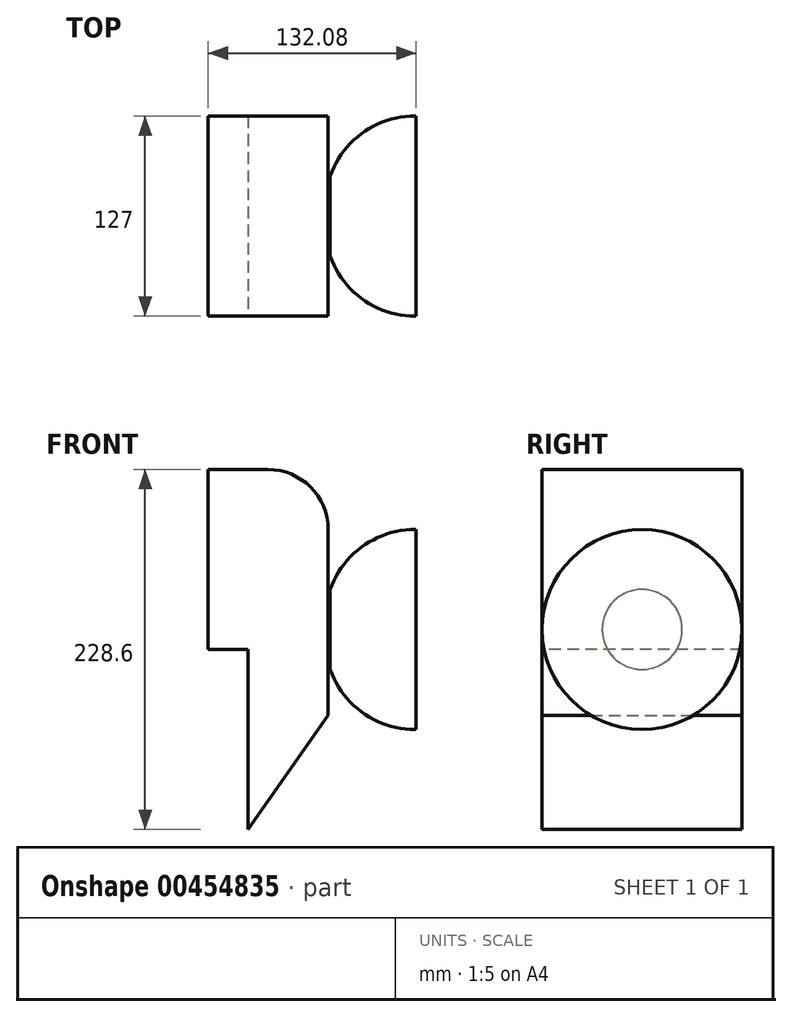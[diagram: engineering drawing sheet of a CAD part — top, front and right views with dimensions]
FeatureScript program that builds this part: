
annotation { "Feature Type Name" : "Feature", "Feature Type Description" : "" }
export const myFeature = defineFeature(function(context is Context, id is Id, definition is map)
    precondition{}
    {
        {
            var Q0;
            Q0=qCreatedBy(makeId("Right.planeOp"),FACE);
            var sketch = newSketch(context, id + "F0", { "sketchPlane" : qUnion([Q0])});
            skLineSegment(sketch, "E0.bottom", {"start": v(63.5, 114.3) * mm, "end": v(-63.5, 114.3) * mm});
            skLineSegment(sketch, "E0.top", {"start": v(63.5, -114.3) * mm, "end": v(-63.5, -114.3) * mm});
            skLineSegment(sketch, "E0.left", {"start": v(63.5, 114.3) * mm, "end": v(63.5, -114.3) * mm});
            skLineSegment(sketch, "E0.right", {"start": v(-63.5, 114.3) * mm, "end": v(-63.5, -114.3) * mm});
            skPoint(sketch, "E0.middle", {"position": v(0, 0) * mm});
            skSolve(sketch);
        }
        {
            var Q0;
            Q0 = qSketchRegion(id + "F0", true);
            extrude(context, id + "F1", {"entities" : qUnion([Q0]), "depth" : 50.8 * mm, "offsetDistance" : 25.4 * mm});
        }
        {
            var Q0;
            Q0=makeQuery(id+"F1.opExtrude","CAP_EDGE",EDGE,{"disambiguationData":[OSD([sQuery(id+"F0.wireOp",EDGE,"E0.bottom")])],"isStart":false});
            fillet(context, id + "F2", {"entities" : qUnion([Q0]), "radius" : 38.1 * mm, "tangentPropagation" : true, "allowEdgeOverflow" : false});
        }
        {
            var Q0;
            Q0=makeQuery(id+"F1.opExtrude","CAP_EDGE",EDGE,{"disambiguationData":[OSD([sQuery(id+"F0.wireOp",EDGE,"E0.top")])],"isStart":false});
            chamfer(context, id + "F3", {"entities" : qUnion([Q0]), "chamferType" : ChamferType.OFFSET_ANGLE, "width" : 50.8 * mm, "oppositeDirection" : false, "angle" : 55 * degree, "tangentPropagation" : true});
        }
        {
            var Q0;
            Q0=makeQuery(id+"F1.opExtrude","CAP_FACE",FACE,{"disambiguationData":[OSD([sQuery(id+"F0.wireOp",EDGE,"E0.bottom"),sQuery(id+"F0.wireOp",EDGE,"E0.top"),sQuery(id+"F0.wireOp",EDGE,"E0.left"),sQuery(id+"F0.wireOp",EDGE,"E0.right")])],"isStart":true});
            var sketch = newSketch(context, id + "F4", { "sketchPlane" : qUnion([Q0])});
            skLineSegment(sketch, "E1.bottom", {"start": v(-63.5, 114.3) * mm, "end": v(63.5, 114.3) * mm});
            skLineSegment(sketch, "E1.top", {"start": v(-63.5, 101.6) * mm, "end": v(63.5, 101.6) * mm});
            skLineSegment(sketch, "E1.left", {"start": v(-63.5, 114.3) * mm, "end": v(-63.5, 101.6) * mm});
            skLineSegment(sketch, "E1.right", {"start": v(63.5, 114.3) * mm, "end": v(63.5, 101.6) * mm});
            skSolve(sketch);
        }
        {
            var Q0;
            Q0 = qSketchRegion(id + "F4", true);
            extrude(context, id + "F5", {"entities" : qUnion([Q0]), "operationType" : NewBodyOperationType.ADD, "depth" : 25.4 * mm, "offsetDistance" : 25.4 * mm});
        }
        {
            var Q0;
            Q0=makeQuery(id+"F1.opExtrude","CAP_FACE",FACE,{"disambiguationData":[OSD([sQuery(id+"F0.wireOp",EDGE,"E0.bottom"),sQuery(id+"F0.wireOp",EDGE,"E0.top"),sQuery(id+"F0.wireOp",EDGE,"E0.left"),sQuery(id+"F0.wireOp",EDGE,"E0.right")])],"isStart":true});
            var sketch = newSketch(context, id + "F6", { "sketchPlane" : qUnion([Q0])});
            skLineSegment(sketch, "E2.bottom", {"start": v(-63.5, 101.6) * mm, "end": v(63.5, 101.6) * mm});
            skLineSegment(sketch, "E2.top", {"start": v(-63.5, 0) * mm, "end": v(63.5, 0) * mm});
            skLineSegment(sketch, "E2.left", {"start": v(-63.5, 101.6) * mm, "end": v(-63.5, 0) * mm});
            skLineSegment(sketch, "E2.right", {"start": v(63.5, 101.6) * mm, "end": v(63.5, 0) * mm});
            skSolve(sketch);
        }
        {
            var Q0;
            Q0 = qSketchRegion(id + "F6", true);
            extrude(context, id + "F7", {"entities" : qUnion([Q0]), "operationType" : NewBodyOperationType.ADD, "depth" : 25.4 * mm, "offsetDistance" : 25.4 * mm});
        }
        {
            var Q0;
            Q0=makeQuery(id+"F1.opExtrude","CAP_FACE",FACE,{"disambiguationData":[OSD([sQuery(id+"F0.wireOp",EDGE,"E0.bottom"),sQuery(id+"F0.wireOp",EDGE,"E0.top"),sQuery(id+"F0.wireOp",EDGE,"E0.left"),sQuery(id+"F0.wireOp",EDGE,"E0.right")])],"isStart":false});
            var sketch = newSketch(context, id + "F8", { "sketchPlane" : qUnion([Q0])});
            skCircle(sketch, "E3", {"center": v(0, 12.7) * mm, "radius": 25.4 * mm});
            skSolve(sketch);
        }
        {
            var Q0;
            Q0 = qSketchRegion(id + "F8", true);
            extrude(context, id + "F9", {"entities" : qUnion([Q0]), "operationType" : NewBodyOperationType.ADD, "depth" : 1.27 * mm, "offsetDistance" : 25.4 * mm});
        }
        {
            var Q0;
            Q0=makeQuery(id+"F9.opExtrude","CAP_FACE",FACE,{"disambiguationData":[OSD([sQuery(id+"F8.wireOp",EDGE,"E3")])],"isStart":false});
            var sketch = newSketch(context, id + "F10", { "sketchPlane" : qUnion([Q0])});
            skCircle(sketch, "E4", {"center": v(0, 12.7) * mm, "radius": 63.5 * mm});
            skSolve(sketch);
        }
        {
            var Q0;
            Q0 = qSketchRegion(id + "F10", true);
            extrude(context, id + "F11", {"entities" : qUnion([Q0]), "operationType" : NewBodyOperationType.ADD, "depth" : 54.6 * mm, "offsetDistance" : 25.4 * mm});
        }
        {
            var Q0;
            Q0=makeQuery(id+"F11.opExtrude","CAP_EDGE",EDGE,{"disambiguationData":[OSD([sQuery(id+"F10.wireOp",EDGE,"E4")])],"isStart":true});
            fillet(context, id + "F12", {"entities" : qUnion([Q0]), "radius" : 57.15 * mm, "tangentPropagation" : true, "allowEdgeOverflow" : false});
        }
    });
